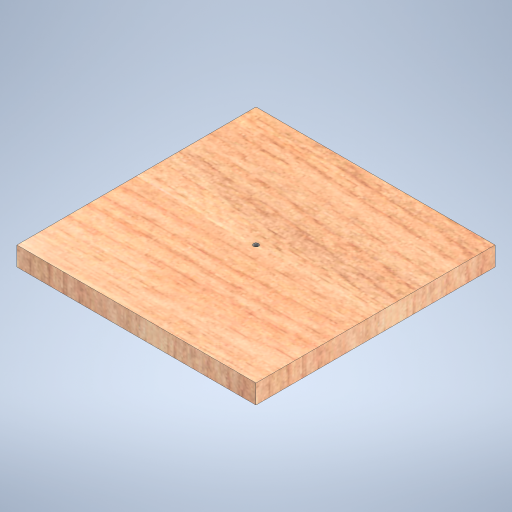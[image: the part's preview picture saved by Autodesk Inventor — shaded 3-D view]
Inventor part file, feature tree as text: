
AUTODESK INVENTOR PART (.ipt)
format: ipt  version: 2024 (Build 280153000, 153)  size: 390,144 bytes
history: native  units: in
note: dims shown in document units (in); Inventor stores cm internally (conversion verified against a paired STEP export)
features: sketch x2, extrude x1, hole x1
ambient origin geometry x8: Origin, YZ Plane, XZ Plane, XY Plane, X Axis, Y Axis, Z Axis, Center Point
bodies: Solid1 (feature_tree)
feature tree (4):
  extrude  "Extrusion1"  Depth=5.9055in
  hole  "Hole1"  [1 undecoded]
  sketch  "Sketch1"  dims[d0=5.9055in d1=5.9055in]
  sketch  "Sketch2"  dims[d2=0.4724in d3=0.0in d4=0.1276in d5=0.315in d6=0.3386in d7=0.0787in d8=90.0deg d9=0.315in d10=0.8108in]
note: 1 required parameter value undecoded (feature->parameter linkage not recoverable at this tier; creation-order binding heuristic only, values carry confidence <= 0.55)
